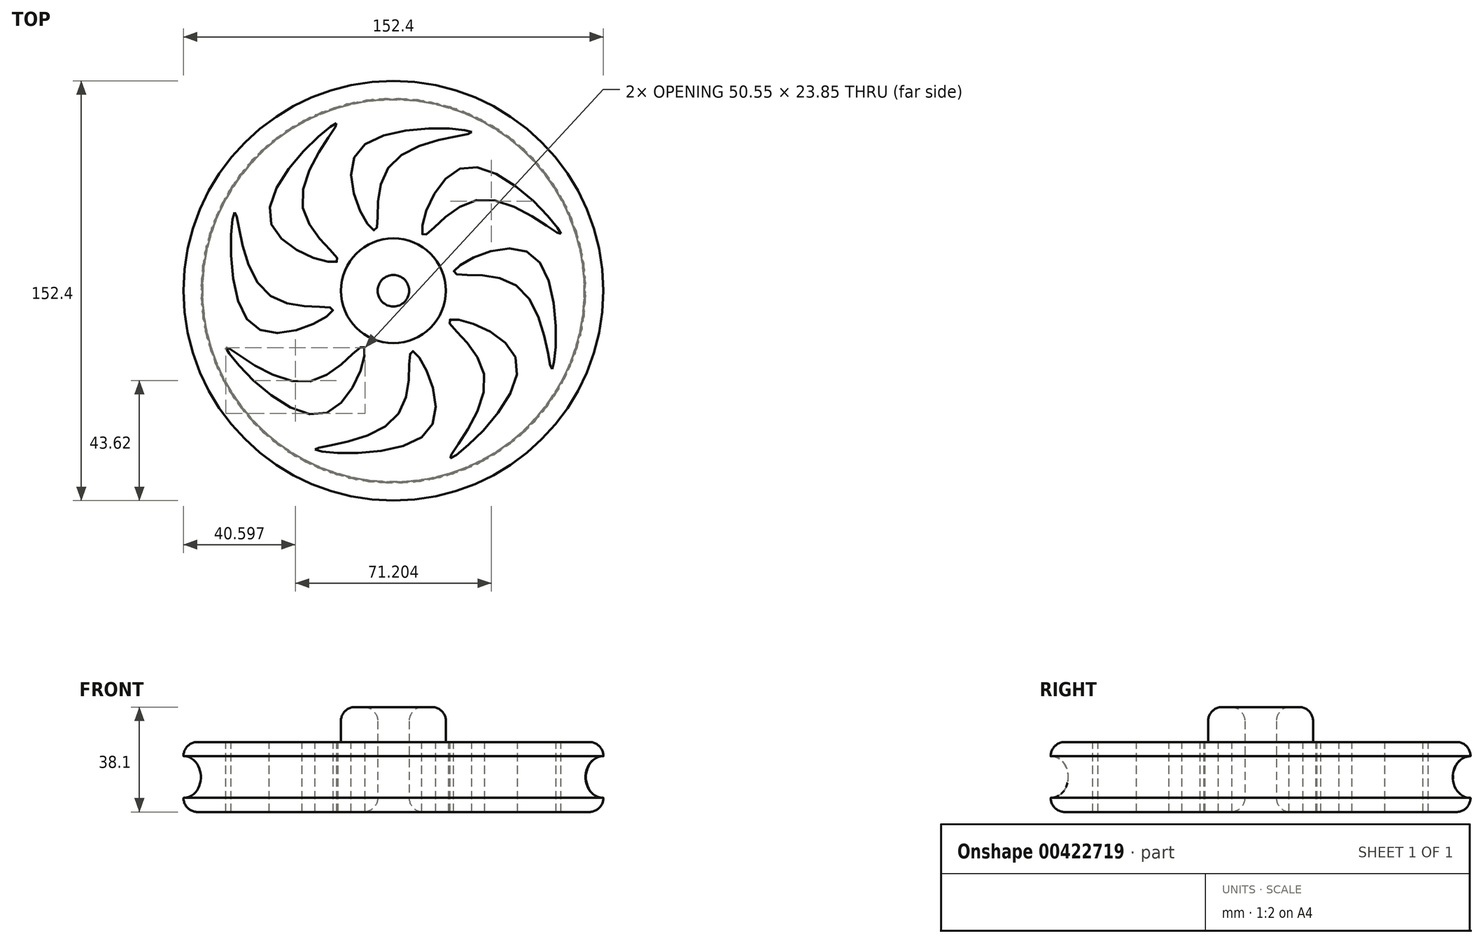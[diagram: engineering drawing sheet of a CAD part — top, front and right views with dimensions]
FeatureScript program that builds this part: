
annotation { "Feature Type Name" : "Feature", "Feature Type Description" : "" }
export const myFeature = defineFeature(function(context is Context, id is Id, definition is map)
    precondition{}
    {
        {
            var Q0;
            Q0=qCreatedBy(makeId("Top.planeOp"),FACE);
            var sketch = newSketch(context, id + "F0", { "sketchPlane" : qUnion([Q0])});
            skCircle(sketch, "E0", {"center": v(42.45, 47.34) * mm, "radius": 76.2 * mm});
            skCircle(sketch, "E1", {"center": v(42.45, 47.34) * mm, "radius": 19.05 * mm});
            skCircle(sketch, "E2", {"center": v(42.45, 47.34) * mm, "radius": 5.72 * mm});
            skSolve(sketch);
        }
        {
            var Q0;
            Q0 = qSketchRegion(id + "F0", true);
            extrude(context, id + "F1", {"entities" : qUnion([Q0]), "depth" : 25.4 * mm});
        }
        {
            var Q0;
            Q0 = qSketchRegion(id + "F0", true);
            extrude(context, id + "F2", {"entities" : qUnion([Q0]), "operationType" : NewBodyOperationType.ADD, "depth" : 25.4 * mm});
        }
        {
            var Q0;
            Q0=makeQuery(id+"F0.imprint","IMPRINT",FACE,{"disambiguationData":[TD([[makeQuery(id+"F0.imprint","IMPRINT",EDGE,{"derivedFrom":sQuery(id+"F0.wireOp",EDGE,"E1")}),1.0]])]});
            extrude(context, id + "F3", {"entities" : qUnion([Q0]), "operationType" : NewBodyOperationType.ADD, "depth" : 38.1 * mm});
        }
        {
            var Q0;
            Q0 = qSketchRegion(id + "F0", true);
            extrude(context, id + "F4", {"entities" : qUnion([Q0]), "operationType" : NewBodyOperationType.ADD, "depth" : 25.4 * mm});
        }
        {
            var Q0;
            Q0=makeQuery(id+"F3.opExtrude","CAP_EDGE",EDGE,{"disambiguationData":[OSD([sQuery(id+"F0.wireOp",EDGE,"E1")])],"isStart":false});
            fillet(context, id + "F5", {"entities" : qUnion([Q0]), "radius" : 5.08 * mm, "tangentPropagation" : true, "allowEdgeOverflow" : false});
        }
        {
            var Q0;
            Q0=makeQuery(id+"F1.opExtrude","CAP_EDGE",EDGE,{"disambiguationData":[OSD([sQuery(id+"F0.wireOp",EDGE,"E0")])],"isStart":false});
            fillet(context, id + "F6", {"entities" : qUnion([Q0]), "radius" : 5.08 * mm, "tangentPropagation" : true, "allowEdgeOverflow" : false});
        }
        {
            var Q0;
            Q0=makeQuery(id+"F1.opExtrude","CAP_EDGE",EDGE,{"disambiguationData":[OSD([sQuery(id+"F0.wireOp",EDGE,"E0")])],"isStart":true});
            fillet(context, id + "F7", {"entities" : qUnion([Q0]), "radius" : 5.08 * mm, "tangentPropagation" : true, "allowEdgeOverflow" : false});
        }
        {
            var Q0;
            Q0=qCreatedBy(makeId("Right.planeOp"),FACE);
            var sketch = newSketch(context, id + "F8", { "sketchPlane" : qUnion([Q0])});
            skCircle(sketch, "E3", {"center": v(-15.75, 12.67) * mm, "radius": 7.56 * mm});
            skPoint(sketch, "E3.first.point", {"position": v(-15.42, 20.22) * mm});
            skPoint(sketch, "E3.second.point", {"position": v(-15.56, 5.12) * mm});
            skPoint(sketch, "E3.third.point", {"position": v(-23.31, 12.74) * mm});
            skSolve(sketch);
        }
        {
            var Q0;
            Q0=makeQuery(id+"F8.imprint","IMPRINT",FACE,{"disambiguationData":[TD([[makeQuery(id+"F8.imprint","IMPRINT",EDGE,{"derivedFrom":sQuery(id+"F8.wireOp",EDGE,"E3")}),1.0]])]});
            var Q1;
            {var subQ0=sQuery(id+"F0.wireOp",EDGE,"E0");Q1=makeQuery(id+"F6.opFillet","BLEND_EDGE",EDGE,{"blendedFrom":[makeQuery(id+"F1.opExtrude","CAP_EDGE",EDGE,{"disambiguationData":[OSD([subQ0])],"isStart":false}),makeQuery(id+"F1.opExtrude","CAP_FACE",FACE,{"disambiguationData":[OSD([subQ0,sQuery(id+"F0.wireOp",EDGE,"E1")])],"isStart":false})],"blendedInto":[makeQuery(id+"F1.opExtrude","CAP_FACE",FACE,{"disambiguationData":[OSD([subQ0,sQuery(id+"F0.wireOp",EDGE,"E1")])],"isStart":false})]});}
            revolve(context, id + "F9", {"operationType" : NewBodyOperationType.REMOVE, "entities" : qUnion([Q0]), "axis" : qUnion([Q1]), "revolveType" : RevolveType.FULL, "oppositeDirection" : true});
        }
        {
            var Q0;
            Q0=makeQuery(id+"F3.opExtrude","CAP_EDGE",EDGE,{"disambiguationData":[OSD([sQuery(id+"F0.wireOp",EDGE,"E2")])],"isStart":false});
            var Q1;
            Q1=makeQuery(id+"F3.opExtrude","CAP_EDGE",EDGE,{"disambiguationData":[OSD([sQuery(id+"F0.wireOp",EDGE,"E2")])],"isStart":true});
            fillet(context, id + "F10", {"entities" : qUnion([Q0, Q1]), "radius" : 5.08 * mm, "tangentPropagation" : true, "allowEdgeOverflow" : false});
        }
        {
            var Q0;
            Q0=makeQuery(id+"F1.opExtrude","CAP_FACE",FACE,{"disambiguationData":[OSD([sQuery(id+"F0.wireOp",EDGE,"E0"),sQuery(id+"F0.wireOp",EDGE,"E1")])],"isStart":false});
            var sketch = newSketch(context, id + "F11", { "sketchPlane" : qUnion([Q0])});
            skFitSpline(sketch, "E4", {"points": [v(-15.2, 75.78) * mm, v(-7.85, 34.13) * mm, v(20.57, 40.5) * mm, v(-3.44, 46.38) * mm, v(-15.2, 75.78) * mm]});
            skSolve(sketch);
        }
        {
            var Q0;
            Q0 = qSketchRegion(id + "F11", true);
            extrude(context, id + "F12", {"entities" : qUnion([Q0]), "operationType" : NewBodyOperationType.REMOVE, "oppositeDirection" : true, "depth" : 25.4 * mm, "offsetDistance" : 25.4 * mm});
        }
        {
            var Q0;
            Q0=makeQuery(id+"F1.opExtrude","SWEPT_BODY",BODY,{"disambiguationData":[OSD([sQuery(id+"F0.wireOp",EDGE,"E0"),sQuery(id+"F0.wireOp",EDGE,"E1")])]});
            var Q1;
            {var subQ0=sQuery(id+"F0.wireOp",EDGE,"E2");Q1=makeQuery(id+"F10.opFillet","BLEND_EDGE",EDGE,{"blendedFrom":[makeQuery(id+"F3.opExtrude","CAP_EDGE",EDGE,{"disambiguationData":[OSD([subQ0])],"isStart":false}),makeQuery(id+"F3.opExtrude","SWEPT_FACE",FACE,{"disambiguationData":[OSD([subQ0])]})],"blendedInto":[makeQuery(id+"F3.opExtrude","SWEPT_FACE",FACE,{"disambiguationData":[OSD([subQ0])]})]});}
            circularPattern(context, id + "F13", {"entities" : qUnion([Q0]), "axis" : qUnion([Q1]), "angle" : 360 * degree, "instanceCount" : 8, "equalSpace" : true});
        }
    });
